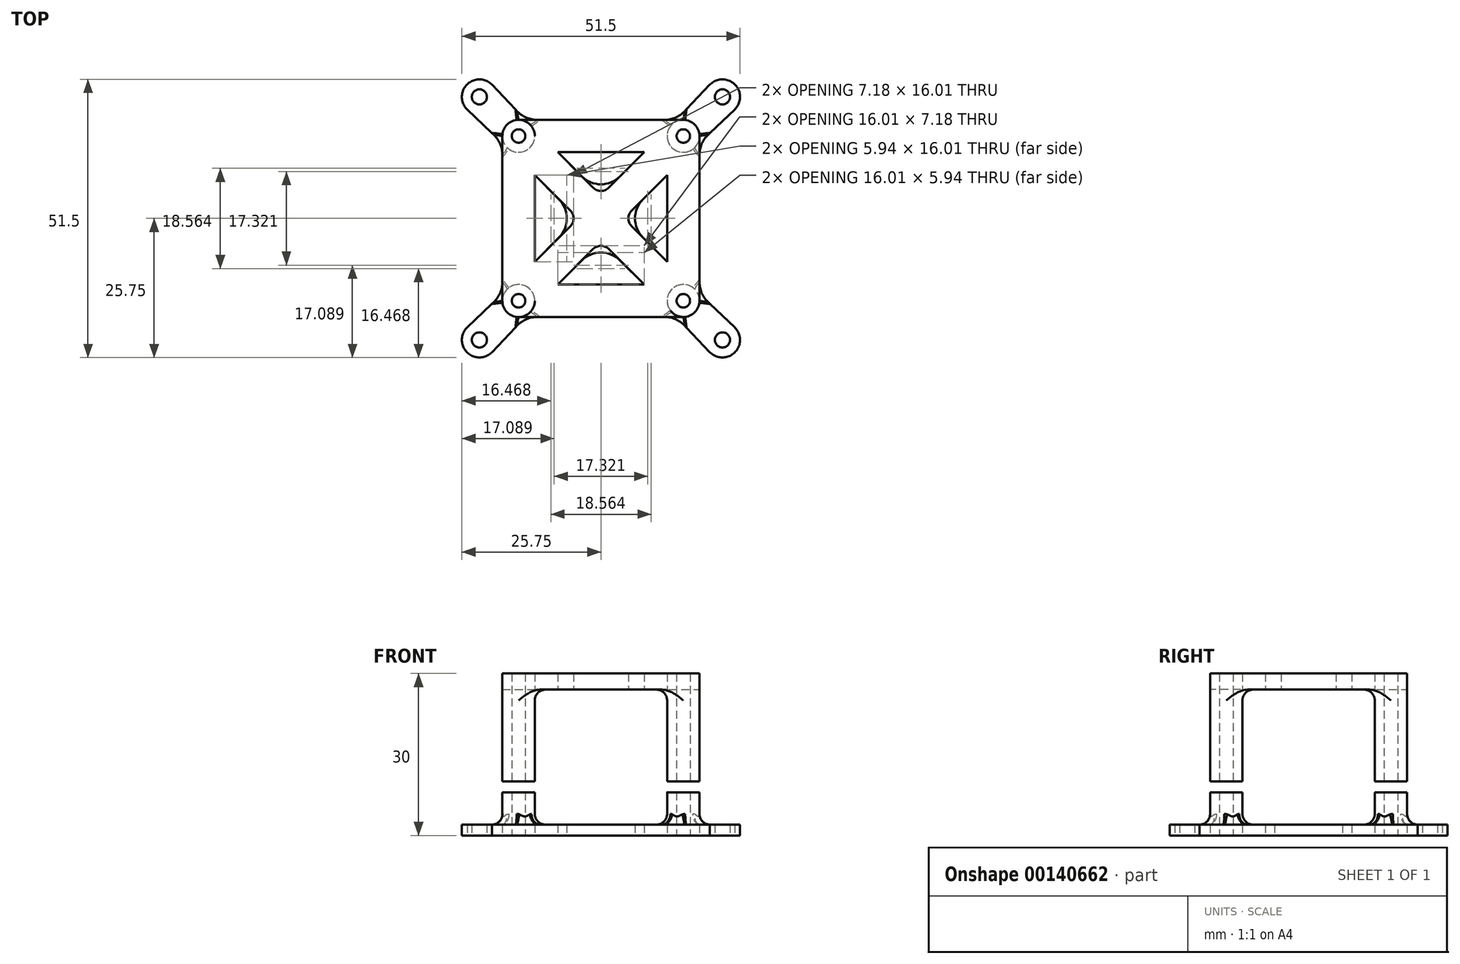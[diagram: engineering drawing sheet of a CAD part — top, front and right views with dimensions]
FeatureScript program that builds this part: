
annotation { "Feature Type Name" : "Feature", "Feature Type Description" : "" }
export const myFeature = defineFeature(function(context is Context, id is Id, definition is map)
    precondition{}
    {
        {
            var Q0;
            Q0=qCreatedBy(makeId("Top.planeOp"),FACE);
            var sketch = newSketch(context, id + "F0", { "sketchPlane" : qUnion([Q0])});
            skPoint(sketch, "E0.middle", {"position": v(0, 0) * mm});
            skPoint(sketch, "E1", {"position": v(-15.25, 15.25) * mm});
            skPoint(sketch, "E2", {"position": v(-22.5, 22.5) * mm});
            skPoint(sketch, "E3", {"position": v(-25, 40) * mm});
            skPoint(sketch, "E4", {"position": v(-25, 60) * mm});
            skCircle(sketch, "E5", {"center": v(0, 0) * mm, "radius": 71 * mm, "construction": true});
            skLineSegment(sketch, "E6", {"start": v(-22.5, 22.5) * mm, "end": v(0, 0) * mm, "construction": true});
            skCircle(sketch, "E7", {"center": v(-22.5, 22.5) * mm, "radius": 1.4 * mm});
            skCircle(sketch, "E8", {"center": v(-15.25, 15.25) * mm, "radius": 1.25 * mm});
            skCircle(sketch, "E9", {"center": v(-15.25, 15.25) * mm, "radius": 3 * mm});
            skCircle(sketch, "E10", {"center": v(-22.5, 22.5) * mm, "radius": 3.25 * mm});
            skLineSegment(sketch, "E11", {"start": v(-20.18, 24.77) * mm, "end": v(-13.08, 17.32) * mm});
            skLineSegment(sketch, "E12.MirrorCS", {"start": v(-24.77, 20.18) * mm, "end": v(-17.32, 13.08) * mm});
            skLineSegment(sketch, "E13", {"start": v(-15.25, 18.25) * mm, "end": v(15.25, 18.25) * mm});
            skLineSegment(sketch, "E14.0", {"start": v(-8, 12.25) * mm, "end": v(8, 12.25) * mm});
            skLineSegment(sketch, "E15.0", {"start": v(-17.37, 13.13) * mm, "end": v(-17.35, 13.1) * mm});
            skLineSegment(sketch, "E16.trimOffspring", {"start": v(-8, 12.25) * mm, "end": v(0, 4.24) * mm});
            skLineSegment(sketch, "E17.trimOffspring", {"start": v(-13.13, 17.37) * mm, "end": v(-13.1, 17.35) * mm});
            skLineSegment(sketch, "E18.trimOffspring", {"start": v(-13.1, 17.35) * mm, "end": v(-13.08, 17.32) * mm});
            skLineSegment(sketch, "E19.1.1", {"start": v(-18.25, -15.25) * mm, "end": v(-18.25, 15.25) * mm});
            skLineSegment(sketch, "E19.1.2", {"start": v(-20.18, -24.77) * mm, "end": v(-13.08, -17.32) * mm});
            skLineSegment(sketch, "E19.1.3", {"start": v(-12.25, -8) * mm, "end": v(-12.25, 8) * mm});
            skLineSegment(sketch, "E19.1.4", {"start": v(-13.13, -17.37) * mm, "end": v(-13.1, -17.35) * mm});
            skPoint(sketch, "E19.1.5", {"position": v(-15.25, -15.25) * mm});
            skCircle(sketch, "E19.1.6", {"center": v(-15.25, -15.25) * mm, "radius": 1.25 * mm});
            skCircle(sketch, "E19.1.7", {"center": v(-22.5, -22.5) * mm, "radius": 1.4 * mm});
            skPoint(sketch, "E19.1.8", {"position": v(-22.5, -22.5) * mm});
            skCircle(sketch, "E19.1.9", {"center": v(-22.5, -22.5) * mm, "radius": 3.25 * mm});
            skCircle(sketch, "E19.1.10", {"center": v(-15.25, -15.25) * mm, "radius": 3 * mm});
            skLineSegment(sketch, "E19.1.11", {"start": v(-22.5, -22.5) * mm, "end": v(0, 0) * mm, "construction": true});
            skLineSegment(sketch, "E19.1.12", {"start": v(-24.77, -20.18) * mm, "end": v(-17.32, -13.08) * mm});
            skLineSegment(sketch, "E19.1.13", {"start": v(-12.25, -8) * mm, "end": v(-4.24, 0) * mm});
            skLineSegment(sketch, "E19.1.18", {"start": v(-17.37, -13.13) * mm, "end": v(-17.35, -13.1) * mm});
            skLineSegment(sketch, "E19.1.20", {"start": v(-17.35, -13.1) * mm, "end": v(-17.32, -13.08) * mm});
            skLineSegment(sketch, "E19.2.1", {"start": v(15.25, -18.25) * mm, "end": v(-15.25, -18.25) * mm});
            skLineSegment(sketch, "E19.2.2", {"start": v(24.77, -20.18) * mm, "end": v(17.32, -13.08) * mm});
            skLineSegment(sketch, "E19.2.3", {"start": v(8, -12.25) * mm, "end": v(-8, -12.25) * mm});
            skLineSegment(sketch, "E19.2.4", {"start": v(17.37, -13.13) * mm, "end": v(17.35, -13.1) * mm});
            skPoint(sketch, "E19.2.5", {"position": v(15.25, -15.25) * mm});
            skCircle(sketch, "E19.2.6", {"center": v(15.25, -15.25) * mm, "radius": 1.25 * mm});
            skCircle(sketch, "E19.2.7", {"center": v(22.5, -22.5) * mm, "radius": 1.4 * mm});
            skPoint(sketch, "E19.2.8", {"position": v(22.5, -22.5) * mm});
            skCircle(sketch, "E19.2.9", {"center": v(22.5, -22.5) * mm, "radius": 3.25 * mm});
            skCircle(sketch, "E19.2.10", {"center": v(15.25, -15.25) * mm, "radius": 3 * mm});
            skLineSegment(sketch, "E19.2.11", {"start": v(22.5, -22.5) * mm, "end": v(0, 0) * mm, "construction": true});
            skLineSegment(sketch, "E19.2.12", {"start": v(20.18, -24.77) * mm, "end": v(13.08, -17.32) * mm});
            skLineSegment(sketch, "E19.2.13", {"start": v(8, -12.25) * mm, "end": v(0, -4.24) * mm});
            skLineSegment(sketch, "E19.2.18", {"start": v(13.13, -17.37) * mm, "end": v(13.1, -17.35) * mm});
            skLineSegment(sketch, "E19.2.20", {"start": v(13.1, -17.35) * mm, "end": v(13.08, -17.32) * mm});
            skLineSegment(sketch, "E19.3.1", {"start": v(18.25, 15.25) * mm, "end": v(18.25, -15.25) * mm});
            skLineSegment(sketch, "E19.3.2", {"start": v(20.18, 24.77) * mm, "end": v(13.08, 17.32) * mm});
            skLineSegment(sketch, "E19.3.3", {"start": v(12.25, 8) * mm, "end": v(12.25, -8) * mm});
            skLineSegment(sketch, "E19.3.4", {"start": v(13.13, 17.37) * mm, "end": v(13.1, 17.35) * mm});
            skPoint(sketch, "E19.3.5", {"position": v(15.25, 15.25) * mm});
            skCircle(sketch, "E19.3.6", {"center": v(15.25, 15.25) * mm, "radius": 1.25 * mm});
            skCircle(sketch, "E19.3.7", {"center": v(22.5, 22.5) * mm, "radius": 1.4 * mm});
            skPoint(sketch, "E19.3.8", {"position": v(22.5, 22.5) * mm});
            skCircle(sketch, "E19.3.9", {"center": v(22.5, 22.5) * mm, "radius": 3.25 * mm});
            skCircle(sketch, "E19.3.10", {"center": v(15.25, 15.25) * mm, "radius": 3 * mm});
            skLineSegment(sketch, "E19.3.11", {"start": v(22.5, 22.5) * mm, "end": v(0, 0) * mm, "construction": true});
            skLineSegment(sketch, "E19.3.12", {"start": v(24.77, 20.18) * mm, "end": v(17.32, 13.08) * mm});
            skLineSegment(sketch, "E19.3.13", {"start": v(12.25, 8) * mm, "end": v(4.24, 0) * mm});
            skLineSegment(sketch, "E19.3.18", {"start": v(17.37, 13.13) * mm, "end": v(17.35, 13.1) * mm});
            skLineSegment(sketch, "E19.3.20", {"start": v(17.35, 13.1) * mm, "end": v(17.32, 13.08) * mm});
            skLineSegment(sketch, "E20.trimOffspring", {"start": v(-12.25, 8) * mm, "end": v(-4.24, 0) * mm});
            skPoint(sketch, "E21.orphan", {"position": v(-2.12, -2.12) * mm});
            skPoint(sketch, "E22.orphan", {"position": v(-2.12, 2.12) * mm});
            skPoint(sketch, "E23.orphan", {"position": v(2.12, 2.12) * mm});
            skPoint(sketch, "E24.orphan", {"position": v(2.12, -2.12) * mm});
            skLineSegment(sketch, "E25.trimOffspring", {"start": v(8, 12.25) * mm, "end": v(0, 4.24) * mm});
            skLineSegment(sketch, "E26.trimOffspring", {"start": v(12.25, -8) * mm, "end": v(4.24, 0) * mm});
            skPoint(sketch, "E27.orphan", {"position": v(12.25, -15.25) * mm});
            skLineSegment(sketch, "E28.trimOffspring", {"start": v(-8, -12.25) * mm, "end": v(0, -4.24) * mm});
            skPoint(sketch, "E29.orphan", {"position": v(-12.25, 15.25) * mm});
            skLineSegment(sketch, "E30.trimOffspring", {"start": v(-17.35, 13.1) * mm, "end": v(-17.32, 13.08) * mm});
            skPoint(sketch, "E31.orphan", {"position": v(-18.25, -13.96) * mm});
            skPoint(sketch, "E32.orphan", {"position": v(13.96, -18.25) * mm});
            skPoint(sketch, "E33.orphan", {"position": v(18.25, 13.96) * mm});
            skPoint(sketch, "E34.orphan", {"position": v(-13.96, 18.25) * mm});
            skSolve(sketch);
        }
        {
            var Q0;
            {var subQ0=sQuery(id+"F0.wireOp",EDGE,"E15.0");Q0=makeQuery(id+"F0.imprint","IMPRINT",FACE,{"disambiguationData":[TD([[makeQuery(id+"F0.imprint","IMPRINT",EDGE,{"derivedFrom":subQ0}),-1.0]])]});}
            var Q1;
            Q1=makeQuery(id+"F0.imprint","IMPRINT",FACE,{"disambiguationData":[TD([[makeQuery(id+"F0.imprint","IMPRINT",EDGE,{"derivedFrom":sQuery(id+"F0.wireOp",EDGE,"E8")}),-1.0]])]});
            var Q2;
            {var subQ3=sQuery(id+"F0.wireOp",EDGE,"E17.trimOffspring");Q2=makeQuery(id+"F0.imprint","IMPRINT",FACE,{"disambiguationData":[TD([[makeQuery(id+"F0.imprint","IMPRINT",EDGE,{"derivedFrom":subQ3}),1.0]])]});}
            var Q3;
            {var subQ0=sQuery(id+"F0.wireOp",EDGE,"E17.trimOffspring");Q3=makeQuery(id+"F0.imprint","IMPRINT",FACE,{"disambiguationData":[TD([[makeQuery(id+"F0.imprint","IMPRINT",EDGE,{"derivedFrom":subQ0}),-1.0]])]});}
            var Q4;
            {var subQ0=sQuery(id+"F0.wireOp",EDGE,"E15.0");Q4=makeQuery(id+"F0.imprint","IMPRINT",FACE,{"disambiguationData":[TD([[makeQuery(id+"F0.imprint","IMPRINT",EDGE,{"derivedFrom":subQ0}),1.0]])]});}
            var Q5;
            Q5=makeQuery(id+"F0.imprint","IMPRINT",FACE,{"disambiguationData":[TD([[makeQuery(id+"F0.imprint","IMPRINT",EDGE,{"derivedFrom":sQuery(id+"F0.wireOp",EDGE,"E19.3.6")}),-1.0]])]});
            var Q6;
            {var subQ5=sQuery(id+"F0.wireOp",EDGE,"E19.3.4");Q6=makeQuery(id+"F0.imprint","IMPRINT",FACE,{"disambiguationData":[TD([[makeQuery(id+"F0.imprint","IMPRINT",EDGE,{"derivedFrom":subQ5}),-1.0]])]});}
            var Q7;
            {var subQ5=sQuery(id+"F0.wireOp",EDGE,"E19.3.18");Q7=makeQuery(id+"F0.imprint","IMPRINT",FACE,{"disambiguationData":[TD([[makeQuery(id+"F0.imprint","IMPRINT",EDGE,{"derivedFrom":subQ5}),1.0]])]});}
            var Q8;
            {var subQ3=sQuery(id+"F0.wireOp",EDGE,"E19.3.4");Q8=makeQuery(id+"F0.imprint","IMPRINT",FACE,{"disambiguationData":[TD([[makeQuery(id+"F0.imprint","IMPRINT",EDGE,{"derivedFrom":subQ3}),1.0]])]});}
            var Q9;
            {var subQ0=sQuery(id+"F0.wireOp",EDGE,"E19.3.18");Q9=makeQuery(id+"F0.imprint","IMPRINT",FACE,{"disambiguationData":[TD([[makeQuery(id+"F0.imprint","IMPRINT",EDGE,{"derivedFrom":subQ0}),-1.0]])]});}
            var Q10;
            Q10=makeQuery(id+"F0.imprint","IMPRINT",FACE,{"disambiguationData":[TD([[makeQuery(id+"F0.imprint","IMPRINT",EDGE,{"derivedFrom":sQuery(id+"F0.wireOp",EDGE,"E19.1.6")}),-1.0]])]});
            var Q11;
            Q11=makeQuery(id+"F0.imprint","IMPRINT",FACE,{"disambiguationData":[TD([[makeQuery(id+"F0.imprint","IMPRINT",EDGE,{"derivedFrom":sQuery(id+"F0.wireOp",EDGE,"E19.2.6")}),-1.0]])]});
            var Q12;
            {var subQ5=sQuery(id+"F0.wireOp",EDGE,"E19.1.18");Q12=makeQuery(id+"F0.imprint","IMPRINT",FACE,{"disambiguationData":[TD([[makeQuery(id+"F0.imprint","IMPRINT",EDGE,{"derivedFrom":subQ5}),1.0]])]});}
            var Q13;
            {var subQ5=sQuery(id+"F0.wireOp",EDGE,"E19.2.18");Q13=makeQuery(id+"F0.imprint","IMPRINT",FACE,{"disambiguationData":[TD([[makeQuery(id+"F0.imprint","IMPRINT",EDGE,{"derivedFrom":subQ5}),1.0]])]});}
            var Q14;
            {var subQ0=sQuery(id+"F0.wireOp",EDGE,"E19.1.4");Q14=makeQuery(id+"F0.imprint","IMPRINT",FACE,{"disambiguationData":[TD([[makeQuery(id+"F0.imprint","IMPRINT",EDGE,{"derivedFrom":subQ0}),-1.0]])]});}
            var Q15;
            {var subQ0=sQuery(id+"F0.wireOp",EDGE,"E19.2.4");Q15=makeQuery(id+"F0.imprint","IMPRINT",FACE,{"disambiguationData":[TD([[makeQuery(id+"F0.imprint","IMPRINT",EDGE,{"derivedFrom":subQ0}),-1.0]])]});}
            var Q16;
            {var subQ3=sQuery(id+"F0.wireOp",EDGE,"E19.2.4");Q16=makeQuery(id+"F0.imprint","IMPRINT",FACE,{"disambiguationData":[TD([[makeQuery(id+"F0.imprint","IMPRINT",EDGE,{"derivedFrom":subQ3}),1.0]])]});}
            var Q17;
            {var subQ3=sQuery(id+"F0.wireOp",EDGE,"E19.1.4");Q17=makeQuery(id+"F0.imprint","IMPRINT",FACE,{"disambiguationData":[TD([[makeQuery(id+"F0.imprint","IMPRINT",EDGE,{"derivedFrom":subQ3}),1.0]])]});}
            var Q18;
            {var subQ0=sQuery(id+"F0.wireOp",EDGE,"E19.1.18");Q18=makeQuery(id+"F0.imprint","IMPRINT",FACE,{"disambiguationData":[TD([[makeQuery(id+"F0.imprint","IMPRINT",EDGE,{"derivedFrom":subQ0}),-1.0]])]});}
            var Q19;
            {var subQ0=sQuery(id+"F0.wireOp",EDGE,"E19.2.18");Q19=makeQuery(id+"F0.imprint","IMPRINT",FACE,{"disambiguationData":[TD([[makeQuery(id+"F0.imprint","IMPRINT",EDGE,{"derivedFrom":subQ0}),-1.0]])]});}
            var Q20;
            Q20=makeQuery(id+"F0.imprint","IMPRINT",FACE,{"disambiguationData":[TD([[makeQuery(id+"F0.imprint","IMPRINT",EDGE,{"derivedFrom":sQuery(id+"F0.wireOp",EDGE,"E14.0")}),1.0]])]});
            var Q21;
            Q21=makeQuery(id+"F0.imprint","IMPRINT",FACE,{"disambiguationData":[TD([[makeQuery(id+"F0.imprint","IMPRINT",EDGE,{"derivedFrom":sQuery(id+"F0.wireOp",EDGE,"E19.1.7")}),-1.0]])]});
            var Q22;
            {var subQ0=sQuery(id+"F0.wireOp",EDGE,"E19.1.10");var subQ1=sQuery(id+"F0.wireOp",EDGE,"E19.1.1");var subQ2=makeQuery(id+"F0.imprint","INTERSECT",VERTEX,{"derivedFrom":[subQ1,subQ0]});Q22=makeQuery(id+"F0.imprint","IMPRINT",FACE,{"disambiguationData":[TD([[makeQuery(id+"F0.imprint","IMPRINT",EDGE,{"disambiguationData":[TD([[subQ2,-1.0]])],"derivedFrom":subQ1}),1.0]])]});}
            var Q23;
            {var subQ7=sQuery(id+"F0.wireOp",EDGE,"E13");var subQ9=sQuery(id+"F0.wireOp",EDGE,"E9");var subQ10=makeQuery(id+"F0.imprint","INTERSECT",VERTEX,{"derivedFrom":[subQ9,subQ7]});Q23=makeQuery(id+"F0.imprint","IMPRINT",FACE,{"disambiguationData":[TD([[makeQuery(id+"F0.imprint","IMPRINT",EDGE,{"disambiguationData":[TD([[subQ10,-1.0]])],"derivedFrom":subQ9}),-1.0]])]});}
            var Q24;
            Q24=makeQuery(id+"F0.imprint","IMPRINT",FACE,{"disambiguationData":[TD([[makeQuery(id+"F0.imprint","IMPRINT",EDGE,{"derivedFrom":sQuery(id+"F0.wireOp",EDGE,"E7")}),-1.0]])]});
            var Q25;
            Q25=makeQuery(id+"F0.imprint","IMPRINT",FACE,{"disambiguationData":[TD([[makeQuery(id+"F0.imprint","IMPRINT",EDGE,{"derivedFrom":sQuery(id+"F0.wireOp",EDGE,"E19.3.7")}),-1.0]])]});
            var Q26;
            {var subQ5=sQuery(id+"F0.wireOp",EDGE,"E13");var subQ7=sQuery(id+"F0.wireOp",EDGE,"E19.3.10");var subQ11=makeQuery(id+"F0.imprint","INTERSECT",VERTEX,{"derivedFrom":[subQ5,subQ7]});Q26=makeQuery(id+"F0.imprint","IMPRINT",FACE,{"disambiguationData":[TD([[makeQuery(id+"F0.imprint","IMPRINT",EDGE,{"disambiguationData":[TD([[subQ11,1.0]])],"derivedFrom":subQ5}),1.0]])]});}
            var Q27;
            {var subQ7=sQuery(id+"F0.wireOp",EDGE,"E19.2.10");var subQ8=sQuery(id+"F0.wireOp",EDGE,"E19.2.1");var subQ9=makeQuery(id+"F0.imprint","INTERSECT",VERTEX,{"derivedFrom":[subQ8,subQ7]});Q27=makeQuery(id+"F0.imprint","IMPRINT",FACE,{"disambiguationData":[TD([[makeQuery(id+"F0.imprint","IMPRINT",EDGE,{"disambiguationData":[TD([[subQ9,-1.0]])],"derivedFrom":subQ8}),1.0]])]});}
            var Q28;
            Q28=makeQuery(id+"F0.imprint","IMPRINT",FACE,{"disambiguationData":[TD([[makeQuery(id+"F0.imprint","IMPRINT",EDGE,{"derivedFrom":sQuery(id+"F0.wireOp",EDGE,"E19.2.7")}),-1.0]])]});
            extrude(context, id + "F1", {"entities" : qUnion([Q0, Q1, Q2, Q3, Q4, Q5, Q6, Q7, Q8, Q9, Q10, Q11, Q12, Q13, Q14, Q15, Q16, Q17, Q18, Q19, Q20, Q21, Q22, Q23, Q24, Q25, Q26, Q27, Q28]), "depth" : 2 * mm});
        }
        {
            var Q0;
            Q0=makeQuery(id+"F0.imprint","IMPRINT",FACE,{"disambiguationData":[TD([[makeQuery(id+"F0.imprint","IMPRINT",EDGE,{"derivedFrom":sQuery(id+"F0.wireOp",EDGE,"E19.1.6")}),-1.0]])]});
            var Q1;
            Q1=makeQuery(id+"F0.imprint","IMPRINT",FACE,{"disambiguationData":[TD([[makeQuery(id+"F0.imprint","IMPRINT",EDGE,{"derivedFrom":sQuery(id+"F0.wireOp",EDGE,"E8")}),-1.0]])]});
            var Q2;
            Q2=makeQuery(id+"F0.imprint","IMPRINT",FACE,{"disambiguationData":[TD([[makeQuery(id+"F0.imprint","IMPRINT",EDGE,{"derivedFrom":sQuery(id+"F0.wireOp",EDGE,"E19.3.6")}),-1.0]])]});
            var Q3;
            Q3=makeQuery(id+"F0.imprint","IMPRINT",FACE,{"disambiguationData":[TD([[makeQuery(id+"F0.imprint","IMPRINT",EDGE,{"derivedFrom":sQuery(id+"F0.wireOp",EDGE,"E19.2.6")}),-1.0]])]});
            extrude(context, id + "F2", {"entities" : qUnion([Q0, Q1, Q2, Q3]), "operationType" : NewBodyOperationType.ADD, "depth" : 8 * mm});
        }
        {
            var Q0;
            Q0=makeQuery(id+"F1.opExtrude","SWEPT_EDGE",EDGE,{"disambiguationData":[OSD([sQuery(id+"F0.wireOp",EDGE,"E13"),sQuery(id+"F0.wireOp",EDGE,"E19.3.2")])]});
            var Q1;
            Q1=makeQuery(id+"F1.opExtrude","SWEPT_EDGE",EDGE,{"disambiguationData":[OSD([sQuery(id+"F0.wireOp",EDGE,"E16.trimOffspring"),sQuery(id+"F0.wireOp",EDGE,"E25.trimOffspring")])]});
            var Q2;
            Q2=makeQuery(id+"F1.opExtrude","SWEPT_EDGE",EDGE,{"disambiguationData":[OSD([sQuery(id+"F0.wireOp",EDGE,"E19.1.13"),sQuery(id+"F0.wireOp",EDGE,"E20.trimOffspring")])]});
            var Q3;
            Q3=makeQuery(id+"F1.opExtrude","SWEPT_EDGE",EDGE,{"disambiguationData":[OSD([sQuery(id+"F0.wireOp",EDGE,"E19.2.13"),sQuery(id+"F0.wireOp",EDGE,"E28.trimOffspring")])]});
            var Q4;
            Q4=makeQuery(id+"F1.opExtrude","SWEPT_EDGE",EDGE,{"disambiguationData":[OSD([sQuery(id+"F0.wireOp",EDGE,"E19.1.2"),sQuery(id+"F0.wireOp",EDGE,"E19.2.1")])]});
            var Q5;
            Q5=makeQuery(id+"F1.opExtrude","SWEPT_EDGE",EDGE,{"disambiguationData":[OSD([sQuery(id+"F0.wireOp",EDGE,"E19.2.1"),sQuery(id+"F0.wireOp",EDGE,"E19.2.12")])]});
            var Q6;
            Q6=makeQuery(id+"F1.opExtrude","SWEPT_EDGE",EDGE,{"disambiguationData":[OSD([sQuery(id+"F0.wireOp",EDGE,"E12.MirrorCS"),sQuery(id+"F0.wireOp",EDGE,"E19.1.1")])]});
            var Q7;
            Q7=makeQuery(id+"F1.opExtrude","SWEPT_EDGE",EDGE,{"disambiguationData":[OSD([sQuery(id+"F0.wireOp",EDGE,"E19.2.2"),sQuery(id+"F0.wireOp",EDGE,"E19.3.1")])]});
            var Q8;
            Q8=makeQuery(id+"F1.opExtrude","SWEPT_EDGE",EDGE,{"disambiguationData":[OSD([sQuery(id+"F0.wireOp",EDGE,"E19.3.13"),sQuery(id+"F0.wireOp",EDGE,"E26.trimOffspring")])]});
            var Q9;
            Q9=makeQuery(id+"F1.opExtrude","SWEPT_EDGE",EDGE,{"disambiguationData":[OSD([sQuery(id+"F0.wireOp",EDGE,"E19.3.1"),sQuery(id+"F0.wireOp",EDGE,"E19.3.12")])]});
            var Q10;
            Q10=makeQuery(id+"F1.opExtrude","SWEPT_EDGE",EDGE,{"disambiguationData":[OSD([sQuery(id+"F0.wireOp",EDGE,"E11"),sQuery(id+"F0.wireOp",EDGE,"E13")])]});
            var Q11;
            Q11=makeQuery(id+"F1.opExtrude","SWEPT_EDGE",EDGE,{"disambiguationData":[OSD([sQuery(id+"F0.wireOp",EDGE,"E19.1.1"),sQuery(id+"F0.wireOp",EDGE,"E19.1.12")])]});
            fillet(context, id + "F3", {"entities" : qUnion([Q0, Q1, Q2, Q3, Q4, Q5, Q6, Q7, Q8, Q9, Q10, Q11]), "radius" : 5 * mm, "tangentPropagation" : true, "allowEdgeOverflow" : false});
        }
        {
            var Q0;
            Q0=makeQuery(id+"F2.boolean.opBoolean","INTERSECT",EDGE,{"derivedFrom":[makeQuery(id+"F1.opExtrude","CAP_FACE",FACE,{"disambiguationData":[OSD([sQuery(id+"F0.wireOp",EDGE,"E7"),sQuery(id+"F0.wireOp",EDGE,"E8"),sQuery(id+"F0.wireOp",EDGE,"E10"),sQuery(id+"F0.wireOp",EDGE,"E11"),sQuery(id+"F0.wireOp",EDGE,"E12.MirrorCS"),sQuery(id+"F0.wireOp",EDGE,"E13"),sQuery(id+"F0.wireOp",EDGE,"E14.0"),sQuery(id+"F0.wireOp",EDGE,"E16.trimOffspring"),sQuery(id+"F0.wireOp",EDGE,"E19.1.1"),sQuery(id+"F0.wireOp",EDGE,"E19.1.2"),sQuery(id+"F0.wireOp",EDGE,"E19.1.3"),sQuery(id+"F0.wireOp",EDGE,"E19.1.6"),sQuery(id+"F0.wireOp",EDGE,"E19.1.7"),sQuery(id+"F0.wireOp",EDGE,"E19.1.9"),sQuery(id+"F0.wireOp",EDGE,"E19.1.12"),sQuery(id+"F0.wireOp",EDGE,"E19.1.13"),sQuery(id+"F0.wireOp",EDGE,"E19.2.1"),sQuery(id+"F0.wireOp",EDGE,"E19.2.2"),sQuery(id+"F0.wireOp",EDGE,"E19.2.3"),sQuery(id+"F0.wireOp",EDGE,"E19.2.6"),sQuery(id+"F0.wireOp",EDGE,"E19.2.7"),sQuery(id+"F0.wireOp",EDGE,"E19.2.9"),sQuery(id+"F0.wireOp",EDGE,"E19.2.12"),sQuery(id+"F0.wireOp",EDGE,"E19.2.13"),sQuery(id+"F0.wireOp",EDGE,"E19.3.1"),sQuery(id+"F0.wireOp",EDGE,"E19.3.2"),sQuery(id+"F0.wireOp",EDGE,"E19.3.3"),sQuery(id+"F0.wireOp",EDGE,"E19.3.6"),sQuery(id+"F0.wireOp",EDGE,"E19.3.7"),sQuery(id+"F0.wireOp",EDGE,"E19.3.9"),sQuery(id+"F0.wireOp",EDGE,"E19.3.12"),sQuery(id+"F0.wireOp",EDGE,"E19.3.13"),sQuery(id+"F0.wireOp",EDGE,"E20.trimOffspring"),sQuery(id+"F0.wireOp",EDGE,"E25.trimOffspring"),sQuery(id+"F0.wireOp",EDGE,"E26.trimOffspring"),sQuery(id+"F0.wireOp",EDGE,"E28.trimOffspring")])],"isStart":false}),makeQuery(id+"F2.opExtrude","SWEPT_FACE",FACE,{"disambiguationData":[OSD([sQuery(id+"F0.wireOp",EDGE,"E9")])]})]});
            var Q1;
            Q1=makeQuery(id+"F2.boolean.opBoolean","INTERSECT",EDGE,{"derivedFrom":[makeQuery(id+"F1.opExtrude","CAP_FACE",FACE,{"disambiguationData":[OSD([sQuery(id+"F0.wireOp",EDGE,"E7"),sQuery(id+"F0.wireOp",EDGE,"E8"),sQuery(id+"F0.wireOp",EDGE,"E10"),sQuery(id+"F0.wireOp",EDGE,"E11"),sQuery(id+"F0.wireOp",EDGE,"E12.MirrorCS"),sQuery(id+"F0.wireOp",EDGE,"E13"),sQuery(id+"F0.wireOp",EDGE,"E14.0"),sQuery(id+"F0.wireOp",EDGE,"E16.trimOffspring"),sQuery(id+"F0.wireOp",EDGE,"E19.1.1"),sQuery(id+"F0.wireOp",EDGE,"E19.1.2"),sQuery(id+"F0.wireOp",EDGE,"E19.1.3"),sQuery(id+"F0.wireOp",EDGE,"E19.1.6"),sQuery(id+"F0.wireOp",EDGE,"E19.1.7"),sQuery(id+"F0.wireOp",EDGE,"E19.1.9"),sQuery(id+"F0.wireOp",EDGE,"E19.1.12"),sQuery(id+"F0.wireOp",EDGE,"E19.1.13"),sQuery(id+"F0.wireOp",EDGE,"E19.2.1"),sQuery(id+"F0.wireOp",EDGE,"E19.2.2"),sQuery(id+"F0.wireOp",EDGE,"E19.2.3"),sQuery(id+"F0.wireOp",EDGE,"E19.2.6"),sQuery(id+"F0.wireOp",EDGE,"E19.2.7"),sQuery(id+"F0.wireOp",EDGE,"E19.2.9"),sQuery(id+"F0.wireOp",EDGE,"E19.2.12"),sQuery(id+"F0.wireOp",EDGE,"E19.2.13"),sQuery(id+"F0.wireOp",EDGE,"E19.3.1"),sQuery(id+"F0.wireOp",EDGE,"E19.3.2"),sQuery(id+"F0.wireOp",EDGE,"E19.3.3"),sQuery(id+"F0.wireOp",EDGE,"E19.3.6"),sQuery(id+"F0.wireOp",EDGE,"E19.3.7"),sQuery(id+"F0.wireOp",EDGE,"E19.3.9"),sQuery(id+"F0.wireOp",EDGE,"E19.3.12"),sQuery(id+"F0.wireOp",EDGE,"E19.3.13"),sQuery(id+"F0.wireOp",EDGE,"E20.trimOffspring"),sQuery(id+"F0.wireOp",EDGE,"E25.trimOffspring"),sQuery(id+"F0.wireOp",EDGE,"E26.trimOffspring"),sQuery(id+"F0.wireOp",EDGE,"E28.trimOffspring")])],"isStart":false}),makeQuery(id+"F2.opExtrude","SWEPT_FACE",FACE,{"disambiguationData":[OSD([sQuery(id+"F0.wireOp",EDGE,"E19.3.10")])]})]});
            var Q2;
            Q2=makeQuery(id+"F2.boolean.opBoolean","INTERSECT",EDGE,{"derivedFrom":[makeQuery(id+"F1.opExtrude","CAP_FACE",FACE,{"disambiguationData":[OSD([sQuery(id+"F0.wireOp",EDGE,"E7"),sQuery(id+"F0.wireOp",EDGE,"E8"),sQuery(id+"F0.wireOp",EDGE,"E10"),sQuery(id+"F0.wireOp",EDGE,"E11"),sQuery(id+"F0.wireOp",EDGE,"E12.MirrorCS"),sQuery(id+"F0.wireOp",EDGE,"E13"),sQuery(id+"F0.wireOp",EDGE,"E14.0"),sQuery(id+"F0.wireOp",EDGE,"E16.trimOffspring"),sQuery(id+"F0.wireOp",EDGE,"E19.1.1"),sQuery(id+"F0.wireOp",EDGE,"E19.1.2"),sQuery(id+"F0.wireOp",EDGE,"E19.1.3"),sQuery(id+"F0.wireOp",EDGE,"E19.1.6"),sQuery(id+"F0.wireOp",EDGE,"E19.1.7"),sQuery(id+"F0.wireOp",EDGE,"E19.1.9"),sQuery(id+"F0.wireOp",EDGE,"E19.1.12"),sQuery(id+"F0.wireOp",EDGE,"E19.1.13"),sQuery(id+"F0.wireOp",EDGE,"E19.2.1"),sQuery(id+"F0.wireOp",EDGE,"E19.2.2"),sQuery(id+"F0.wireOp",EDGE,"E19.2.3"),sQuery(id+"F0.wireOp",EDGE,"E19.2.6"),sQuery(id+"F0.wireOp",EDGE,"E19.2.7"),sQuery(id+"F0.wireOp",EDGE,"E19.2.9"),sQuery(id+"F0.wireOp",EDGE,"E19.2.12"),sQuery(id+"F0.wireOp",EDGE,"E19.2.13"),sQuery(id+"F0.wireOp",EDGE,"E19.3.1"),sQuery(id+"F0.wireOp",EDGE,"E19.3.2"),sQuery(id+"F0.wireOp",EDGE,"E19.3.3"),sQuery(id+"F0.wireOp",EDGE,"E19.3.6"),sQuery(id+"F0.wireOp",EDGE,"E19.3.7"),sQuery(id+"F0.wireOp",EDGE,"E19.3.9"),sQuery(id+"F0.wireOp",EDGE,"E19.3.12"),sQuery(id+"F0.wireOp",EDGE,"E19.3.13"),sQuery(id+"F0.wireOp",EDGE,"E20.trimOffspring"),sQuery(id+"F0.wireOp",EDGE,"E25.trimOffspring"),sQuery(id+"F0.wireOp",EDGE,"E26.trimOffspring"),sQuery(id+"F0.wireOp",EDGE,"E28.trimOffspring")])],"isStart":false}),makeQuery(id+"F2.opExtrude","SWEPT_FACE",FACE,{"disambiguationData":[OSD([sQuery(id+"F0.wireOp",EDGE,"E19.1.10")])]})]});
            var Q3;
            Q3=makeQuery(id+"F2.boolean.opBoolean","INTERSECT",EDGE,{"derivedFrom":[makeQuery(id+"F1.opExtrude","CAP_FACE",FACE,{"disambiguationData":[OSD([sQuery(id+"F0.wireOp",EDGE,"E7"),sQuery(id+"F0.wireOp",EDGE,"E8"),sQuery(id+"F0.wireOp",EDGE,"E10"),sQuery(id+"F0.wireOp",EDGE,"E11"),sQuery(id+"F0.wireOp",EDGE,"E12.MirrorCS"),sQuery(id+"F0.wireOp",EDGE,"E13"),sQuery(id+"F0.wireOp",EDGE,"E14.0"),sQuery(id+"F0.wireOp",EDGE,"E16.trimOffspring"),sQuery(id+"F0.wireOp",EDGE,"E19.1.1"),sQuery(id+"F0.wireOp",EDGE,"E19.1.2"),sQuery(id+"F0.wireOp",EDGE,"E19.1.3"),sQuery(id+"F0.wireOp",EDGE,"E19.1.6"),sQuery(id+"F0.wireOp",EDGE,"E19.1.7"),sQuery(id+"F0.wireOp",EDGE,"E19.1.9"),sQuery(id+"F0.wireOp",EDGE,"E19.1.12"),sQuery(id+"F0.wireOp",EDGE,"E19.1.13"),sQuery(id+"F0.wireOp",EDGE,"E19.2.1"),sQuery(id+"F0.wireOp",EDGE,"E19.2.2"),sQuery(id+"F0.wireOp",EDGE,"E19.2.3"),sQuery(id+"F0.wireOp",EDGE,"E19.2.6"),sQuery(id+"F0.wireOp",EDGE,"E19.2.7"),sQuery(id+"F0.wireOp",EDGE,"E19.2.9"),sQuery(id+"F0.wireOp",EDGE,"E19.2.12"),sQuery(id+"F0.wireOp",EDGE,"E19.2.13"),sQuery(id+"F0.wireOp",EDGE,"E19.3.1"),sQuery(id+"F0.wireOp",EDGE,"E19.3.2"),sQuery(id+"F0.wireOp",EDGE,"E19.3.3"),sQuery(id+"F0.wireOp",EDGE,"E19.3.6"),sQuery(id+"F0.wireOp",EDGE,"E19.3.7"),sQuery(id+"F0.wireOp",EDGE,"E19.3.9"),sQuery(id+"F0.wireOp",EDGE,"E19.3.12"),sQuery(id+"F0.wireOp",EDGE,"E19.3.13"),sQuery(id+"F0.wireOp",EDGE,"E20.trimOffspring"),sQuery(id+"F0.wireOp",EDGE,"E25.trimOffspring"),sQuery(id+"F0.wireOp",EDGE,"E26.trimOffspring"),sQuery(id+"F0.wireOp",EDGE,"E28.trimOffspring")])],"isStart":false}),makeQuery(id+"F2.opExtrude","SWEPT_FACE",FACE,{"disambiguationData":[OSD([sQuery(id+"F0.wireOp",EDGE,"E19.2.10")])]})]});
            fillet(context, id + "F4", {"entities" : qUnion([Q0, Q1, Q2, Q3]), "radius" : 2 * mm, "tangentPropagation" : true, "allowEdgeOverflow" : false});
        }
        {
            var Q0;
            Q0=makeQuery(id+"F0.imprint","IMPRINT",FACE,{"disambiguationData":[TD([[makeQuery(id+"F0.imprint","IMPRINT",EDGE,{"derivedFrom":sQuery(id+"F0.wireOp",EDGE,"E19.3.6")}),-1.0]])]});
            var Q1;
            Q1=makeQuery(id+"F0.imprint","IMPRINT",FACE,{"disambiguationData":[TD([[makeQuery(id+"F0.imprint","IMPRINT",EDGE,{"derivedFrom":sQuery(id+"F0.wireOp",EDGE,"E19.2.6")}),-1.0]])]});
            var Q2;
            {var subQ0=sQuery(id+"F0.wireOp",EDGE,"E19.2.4");Q2=makeQuery(id+"F0.imprint","IMPRINT",FACE,{"disambiguationData":[TD([[makeQuery(id+"F0.imprint","IMPRINT",EDGE,{"derivedFrom":subQ0}),-1.0]])]});}
            var Q3;
            {var subQ5=sQuery(id+"F0.wireOp",EDGE,"E19.3.4");Q3=makeQuery(id+"F0.imprint","IMPRINT",FACE,{"disambiguationData":[TD([[makeQuery(id+"F0.imprint","IMPRINT",EDGE,{"derivedFrom":subQ5}),-1.0]])]});}
            var Q4;
            {var subQ5=sQuery(id+"F0.wireOp",EDGE,"E19.3.18");Q4=makeQuery(id+"F0.imprint","IMPRINT",FACE,{"disambiguationData":[TD([[makeQuery(id+"F0.imprint","IMPRINT",EDGE,{"derivedFrom":subQ5}),1.0]])]});}
            var Q5;
            {var subQ3=sQuery(id+"F0.wireOp",EDGE,"E17.trimOffspring");Q5=makeQuery(id+"F0.imprint","IMPRINT",FACE,{"disambiguationData":[TD([[makeQuery(id+"F0.imprint","IMPRINT",EDGE,{"derivedFrom":subQ3}),1.0]])]});}
            var Q6;
            {var subQ0=sQuery(id+"F0.wireOp",EDGE,"E19.1.4");Q6=makeQuery(id+"F0.imprint","IMPRINT",FACE,{"disambiguationData":[TD([[makeQuery(id+"F0.imprint","IMPRINT",EDGE,{"derivedFrom":subQ0}),-1.0]])]});}
            var Q7;
            {var subQ5=sQuery(id+"F0.wireOp",EDGE,"E19.2.18");Q7=makeQuery(id+"F0.imprint","IMPRINT",FACE,{"disambiguationData":[TD([[makeQuery(id+"F0.imprint","IMPRINT",EDGE,{"derivedFrom":subQ5}),1.0]])]});}
            var Q8;
            {var subQ3=sQuery(id+"F0.wireOp",EDGE,"E19.3.4");Q8=makeQuery(id+"F0.imprint","IMPRINT",FACE,{"disambiguationData":[TD([[makeQuery(id+"F0.imprint","IMPRINT",EDGE,{"derivedFrom":subQ3}),1.0]])]});}
            var Q9;
            {var subQ3=sQuery(id+"F0.wireOp",EDGE,"E19.2.4");Q9=makeQuery(id+"F0.imprint","IMPRINT",FACE,{"disambiguationData":[TD([[makeQuery(id+"F0.imprint","IMPRINT",EDGE,{"derivedFrom":subQ3}),1.0]])]});}
            var Q10;
            {var subQ3=sQuery(id+"F0.wireOp",EDGE,"E19.1.4");Q10=makeQuery(id+"F0.imprint","IMPRINT",FACE,{"disambiguationData":[TD([[makeQuery(id+"F0.imprint","IMPRINT",EDGE,{"derivedFrom":subQ3}),1.0]])]});}
            var Q11;
            {var subQ0=sQuery(id+"F0.wireOp",EDGE,"E17.trimOffspring");Q11=makeQuery(id+"F0.imprint","IMPRINT",FACE,{"disambiguationData":[TD([[makeQuery(id+"F0.imprint","IMPRINT",EDGE,{"derivedFrom":subQ0}),-1.0]])]});}
            var Q12;
            {var subQ0=sQuery(id+"F0.wireOp",EDGE,"E19.2.18");Q12=makeQuery(id+"F0.imprint","IMPRINT",FACE,{"disambiguationData":[TD([[makeQuery(id+"F0.imprint","IMPRINT",EDGE,{"derivedFrom":subQ0}),-1.0]])]});}
            var Q13;
            {var subQ0=sQuery(id+"F0.wireOp",EDGE,"E15.0");Q13=makeQuery(id+"F0.imprint","IMPRINT",FACE,{"disambiguationData":[TD([[makeQuery(id+"F0.imprint","IMPRINT",EDGE,{"derivedFrom":subQ0}),1.0]])]});}
            var Q14;
            {var subQ0=sQuery(id+"F0.wireOp",EDGE,"E19.1.18");Q14=makeQuery(id+"F0.imprint","IMPRINT",FACE,{"disambiguationData":[TD([[makeQuery(id+"F0.imprint","IMPRINT",EDGE,{"derivedFrom":subQ0}),-1.0]])]});}
            var Q15;
            {var subQ0=sQuery(id+"F0.wireOp",EDGE,"E19.3.18");Q15=makeQuery(id+"F0.imprint","IMPRINT",FACE,{"disambiguationData":[TD([[makeQuery(id+"F0.imprint","IMPRINT",EDGE,{"derivedFrom":subQ0}),-1.0]])]});}
            var Q16;
            Q16=makeQuery(id+"F0.imprint","IMPRINT",FACE,{"disambiguationData":[TD([[makeQuery(id+"F0.imprint","IMPRINT",EDGE,{"derivedFrom":sQuery(id+"F0.wireOp",EDGE,"E8")}),-1.0]])]});
            var Q17;
            Q17=makeQuery(id+"F0.imprint","IMPRINT",FACE,{"disambiguationData":[TD([[makeQuery(id+"F0.imprint","IMPRINT",EDGE,{"derivedFrom":sQuery(id+"F0.wireOp",EDGE,"E19.1.6")}),-1.0]])]});
            var Q18;
            Q18=makeQuery(id+"F0.imprint","IMPRINT",FACE,{"disambiguationData":[TD([[makeQuery(id+"F0.imprint","IMPRINT",EDGE,{"derivedFrom":sQuery(id+"F0.wireOp",EDGE,"E14.0")}),1.0]])]});
            var Q19;
            {var subQ0=sQuery(id+"F0.wireOp",EDGE,"E15.0");Q19=makeQuery(id+"F0.imprint","IMPRINT",FACE,{"disambiguationData":[TD([[makeQuery(id+"F0.imprint","IMPRINT",EDGE,{"derivedFrom":subQ0}),-1.0]])]});}
            var Q20;
            {var subQ5=sQuery(id+"F0.wireOp",EDGE,"E19.1.18");Q20=makeQuery(id+"F0.imprint","IMPRINT",FACE,{"disambiguationData":[TD([[makeQuery(id+"F0.imprint","IMPRINT",EDGE,{"derivedFrom":subQ5}),1.0]])]});}
            extrude(context, id + "F5", {"entities" : qUnion([Q0, Q1, Q2, Q3, Q4, Q5, Q6, Q7, Q8, Q9, Q10, Q11, Q12, Q13, Q14, Q15, Q16, Q17, Q18, Q19, Q20]), "depth" : 30 * mm, "hasSecondDirection" : true, "secondDirectionOppositeDirection" : false, "secondDirectionDepth" : 27 * mm});
        }
        {
            var Q0;
            Q0=makeQuery(id+"F0.imprint","IMPRINT",FACE,{"disambiguationData":[TD([[makeQuery(id+"F0.imprint","IMPRINT",EDGE,{"derivedFrom":sQuery(id+"F0.wireOp",EDGE,"E19.1.6")}),-1.0]])]});
            var Q1;
            Q1=makeQuery(id+"F0.imprint","IMPRINT",FACE,{"disambiguationData":[TD([[makeQuery(id+"F0.imprint","IMPRINT",EDGE,{"derivedFrom":sQuery(id+"F0.wireOp",EDGE,"E19.2.6")}),-1.0]])]});
            var Q2;
            Q2=makeQuery(id+"F0.imprint","IMPRINT",FACE,{"disambiguationData":[TD([[makeQuery(id+"F0.imprint","IMPRINT",EDGE,{"derivedFrom":sQuery(id+"F0.wireOp",EDGE,"E19.3.6")}),-1.0]])]});
            var Q3;
            Q3=makeQuery(id+"F0.imprint","IMPRINT",FACE,{"disambiguationData":[TD([[makeQuery(id+"F0.imprint","IMPRINT",EDGE,{"derivedFrom":sQuery(id+"F0.wireOp",EDGE,"E8")}),-1.0]])]});
            extrude(context, id + "F6", {"entities" : qUnion([Q0, Q1, Q2, Q3]), "operationType" : NewBodyOperationType.ADD, "depth" : 30 * mm, "hasSecondDirection" : true, "secondDirectionOppositeDirection" : false, "secondDirectionDepth" : 10 * mm});
        }
        {
            var Q0;
            {var subQ0=sQuery(id+"F0.wireOp",EDGE,"E19.3.10");Q0=makeQuery(id+"F6.boolean.opBoolean","INTERSECT",EDGE,{"derivedFrom":[makeQuery(id+"F5.opExtrude","CAP_FACE",FACE,{"disambiguationData":[OSD([sQuery(id+"F0.wireOp",EDGE,"E8"),sQuery(id+"F0.wireOp",EDGE,"E9"),sQuery(id+"F0.wireOp",EDGE,"E13"),sQuery(id+"F0.wireOp",EDGE,"E14.0"),sQuery(id+"F0.wireOp",EDGE,"E16.trimOffspring"),sQuery(id+"F0.wireOp",EDGE,"E19.1.1"),sQuery(id+"F0.wireOp",EDGE,"E19.1.3"),sQuery(id+"F0.wireOp",EDGE,"E19.1.6"),sQuery(id+"F0.wireOp",EDGE,"E19.1.10"),sQuery(id+"F0.wireOp",EDGE,"E19.1.13"),sQuery(id+"F0.wireOp",EDGE,"E19.2.1"),sQuery(id+"F0.wireOp",EDGE,"E19.2.3"),sQuery(id+"F0.wireOp",EDGE,"E19.2.6"),sQuery(id+"F0.wireOp",EDGE,"E19.2.10"),sQuery(id+"F0.wireOp",EDGE,"E19.2.13"),sQuery(id+"F0.wireOp",EDGE,"E19.3.1"),sQuery(id+"F0.wireOp",EDGE,"E19.3.3"),sQuery(id+"F0.wireOp",EDGE,"E19.3.6"),subQ0,sQuery(id+"F0.wireOp",EDGE,"E19.3.13"),sQuery(id+"F0.wireOp",EDGE,"E20.trimOffspring"),sQuery(id+"F0.wireOp",EDGE,"E25.trimOffspring"),sQuery(id+"F0.wireOp",EDGE,"E26.trimOffspring"),sQuery(id+"F0.wireOp",EDGE,"E28.trimOffspring")])],"isStart":true}),makeQuery(id+"F6.opExtrude","SWEPT_FACE",FACE,{"disambiguationData":[OSD([subQ0])]})]});}
            var Q1;
            {var subQ0=sQuery(id+"F0.wireOp",EDGE,"E19.2.10");Q1=makeQuery(id+"F6.boolean.opBoolean","INTERSECT",EDGE,{"derivedFrom":[makeQuery(id+"F5.opExtrude","CAP_FACE",FACE,{"disambiguationData":[OSD([sQuery(id+"F0.wireOp",EDGE,"E8"),sQuery(id+"F0.wireOp",EDGE,"E9"),sQuery(id+"F0.wireOp",EDGE,"E13"),sQuery(id+"F0.wireOp",EDGE,"E14.0"),sQuery(id+"F0.wireOp",EDGE,"E16.trimOffspring"),sQuery(id+"F0.wireOp",EDGE,"E19.1.1"),sQuery(id+"F0.wireOp",EDGE,"E19.1.3"),sQuery(id+"F0.wireOp",EDGE,"E19.1.6"),sQuery(id+"F0.wireOp",EDGE,"E19.1.10"),sQuery(id+"F0.wireOp",EDGE,"E19.1.13"),sQuery(id+"F0.wireOp",EDGE,"E19.2.1"),sQuery(id+"F0.wireOp",EDGE,"E19.2.3"),sQuery(id+"F0.wireOp",EDGE,"E19.2.6"),subQ0,sQuery(id+"F0.wireOp",EDGE,"E19.2.13"),sQuery(id+"F0.wireOp",EDGE,"E19.3.1"),sQuery(id+"F0.wireOp",EDGE,"E19.3.3"),sQuery(id+"F0.wireOp",EDGE,"E19.3.6"),sQuery(id+"F0.wireOp",EDGE,"E19.3.10"),sQuery(id+"F0.wireOp",EDGE,"E19.3.13"),sQuery(id+"F0.wireOp",EDGE,"E20.trimOffspring"),sQuery(id+"F0.wireOp",EDGE,"E25.trimOffspring"),sQuery(id+"F0.wireOp",EDGE,"E26.trimOffspring"),sQuery(id+"F0.wireOp",EDGE,"E28.trimOffspring")])],"isStart":true}),makeQuery(id+"F6.opExtrude","SWEPT_FACE",FACE,{"disambiguationData":[OSD([subQ0])]})]});}
            var Q2;
            {var subQ0=sQuery(id+"F0.wireOp",EDGE,"E19.1.10");Q2=makeQuery(id+"F6.boolean.opBoolean","INTERSECT",EDGE,{"derivedFrom":[makeQuery(id+"F5.opExtrude","CAP_FACE",FACE,{"disambiguationData":[OSD([sQuery(id+"F0.wireOp",EDGE,"E8"),sQuery(id+"F0.wireOp",EDGE,"E9"),sQuery(id+"F0.wireOp",EDGE,"E13"),sQuery(id+"F0.wireOp",EDGE,"E14.0"),sQuery(id+"F0.wireOp",EDGE,"E16.trimOffspring"),sQuery(id+"F0.wireOp",EDGE,"E19.1.1"),sQuery(id+"F0.wireOp",EDGE,"E19.1.3"),sQuery(id+"F0.wireOp",EDGE,"E19.1.6"),subQ0,sQuery(id+"F0.wireOp",EDGE,"E19.1.13"),sQuery(id+"F0.wireOp",EDGE,"E19.2.1"),sQuery(id+"F0.wireOp",EDGE,"E19.2.3"),sQuery(id+"F0.wireOp",EDGE,"E19.2.6"),sQuery(id+"F0.wireOp",EDGE,"E19.2.10"),sQuery(id+"F0.wireOp",EDGE,"E19.2.13"),sQuery(id+"F0.wireOp",EDGE,"E19.3.1"),sQuery(id+"F0.wireOp",EDGE,"E19.3.3"),sQuery(id+"F0.wireOp",EDGE,"E19.3.6"),sQuery(id+"F0.wireOp",EDGE,"E19.3.10"),sQuery(id+"F0.wireOp",EDGE,"E19.3.13"),sQuery(id+"F0.wireOp",EDGE,"E20.trimOffspring"),sQuery(id+"F0.wireOp",EDGE,"E25.trimOffspring"),sQuery(id+"F0.wireOp",EDGE,"E26.trimOffspring"),sQuery(id+"F0.wireOp",EDGE,"E28.trimOffspring")])],"isStart":true}),makeQuery(id+"F6.opExtrude","SWEPT_FACE",FACE,{"disambiguationData":[OSD([subQ0])]})]});}
            var Q3;
            {var subQ0=sQuery(id+"F0.wireOp",EDGE,"E9");Q3=makeQuery(id+"F6.boolean.opBoolean","INTERSECT",EDGE,{"derivedFrom":[makeQuery(id+"F5.opExtrude","CAP_FACE",FACE,{"disambiguationData":[OSD([sQuery(id+"F0.wireOp",EDGE,"E8"),subQ0,sQuery(id+"F0.wireOp",EDGE,"E13"),sQuery(id+"F0.wireOp",EDGE,"E14.0"),sQuery(id+"F0.wireOp",EDGE,"E16.trimOffspring"),sQuery(id+"F0.wireOp",EDGE,"E19.1.1"),sQuery(id+"F0.wireOp",EDGE,"E19.1.3"),sQuery(id+"F0.wireOp",EDGE,"E19.1.6"),sQuery(id+"F0.wireOp",EDGE,"E19.1.10"),sQuery(id+"F0.wireOp",EDGE,"E19.1.13"),sQuery(id+"F0.wireOp",EDGE,"E19.2.1"),sQuery(id+"F0.wireOp",EDGE,"E19.2.3"),sQuery(id+"F0.wireOp",EDGE,"E19.2.6"),sQuery(id+"F0.wireOp",EDGE,"E19.2.10"),sQuery(id+"F0.wireOp",EDGE,"E19.2.13"),sQuery(id+"F0.wireOp",EDGE,"E19.3.1"),sQuery(id+"F0.wireOp",EDGE,"E19.3.3"),sQuery(id+"F0.wireOp",EDGE,"E19.3.6"),sQuery(id+"F0.wireOp",EDGE,"E19.3.10"),sQuery(id+"F0.wireOp",EDGE,"E19.3.13"),sQuery(id+"F0.wireOp",EDGE,"E20.trimOffspring"),sQuery(id+"F0.wireOp",EDGE,"E25.trimOffspring"),sQuery(id+"F0.wireOp",EDGE,"E26.trimOffspring"),sQuery(id+"F0.wireOp",EDGE,"E28.trimOffspring")])],"isStart":true}),makeQuery(id+"F6.opExtrude","SWEPT_FACE",FACE,{"disambiguationData":[OSD([subQ0])]})]});}
            var Q4;
            Q4=makeQuery(id+"F5.opExtrude","SWEPT_EDGE",EDGE,{"disambiguationData":[OSD([sQuery(id+"F0.wireOp",EDGE,"E19.2.13"),sQuery(id+"F0.wireOp",EDGE,"E28.trimOffspring")])]});
            var Q5;
            Q5=makeQuery(id+"F5.opExtrude","SWEPT_EDGE",EDGE,{"disambiguationData":[OSD([sQuery(id+"F0.wireOp",EDGE,"E19.1.13"),sQuery(id+"F0.wireOp",EDGE,"E20.trimOffspring")])]});
            var Q6;
            Q6=makeQuery(id+"F5.opExtrude","SWEPT_EDGE",EDGE,{"disambiguationData":[OSD([sQuery(id+"F0.wireOp",EDGE,"E16.trimOffspring"),sQuery(id+"F0.wireOp",EDGE,"E25.trimOffspring")])]});
            var Q7;
            Q7=makeQuery(id+"F5.opExtrude","SWEPT_EDGE",EDGE,{"disambiguationData":[OSD([sQuery(id+"F0.wireOp",EDGE,"E19.3.13"),sQuery(id+"F0.wireOp",EDGE,"E26.trimOffspring")])]});
            fillet(context, id + "F7", {"entities" : qUnion([Q0, Q1, Q2, Q3, Q4, Q5, Q6, Q7]), "radius" : 2 * mm, "tangentPropagation" : true, "allowEdgeOverflow" : false});
        }
    });
